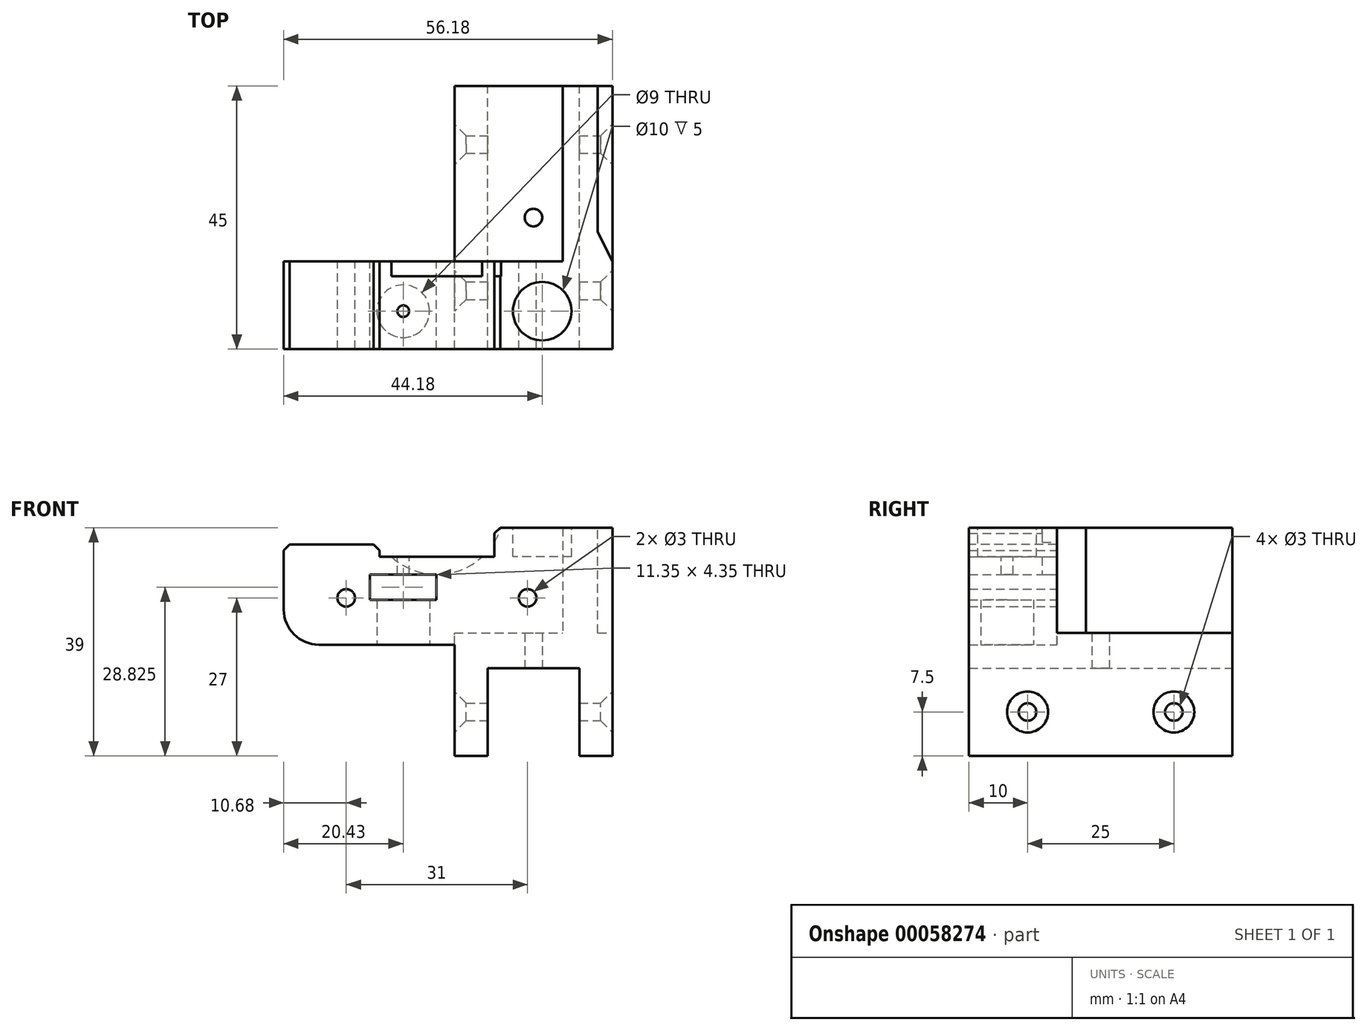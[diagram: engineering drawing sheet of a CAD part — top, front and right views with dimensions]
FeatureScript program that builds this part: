
annotation { "Feature Type Name" : "Feature", "Feature Type Description" : "" }
export const myFeature = defineFeature(function(context is Context, id is Id, definition is map)
    precondition{}
    {
        {
            var Q0;
            Q0=qCreatedBy(makeId("Front.planeOp"),FACE);
            var sketch = newSketch(context, id + "F0", { "sketchPlane" : qUnion([Q0])});
            skLineSegment(sketch, "E0", {"start": v(0, 0) * mm, "end": v(31, 0) * mm, "construction": true});
            skLineSegment(sketch, "E1", {"start": v(0, 0) * mm, "end": v(0, 31) * mm, "construction": true});
            skPoint(sketch, "E2", {"position": v(0, 10.1) * mm});
            skCircle(sketch, "E3", {"center": v(0, 0) * mm, "radius": 1.5 * mm});
            skCircle(sketch, "E4", {"center": v(31, 0) * mm, "radius": 1.5 * mm});
            skLineSegment(sketch, "E5", {"start": v(15.5, 0) * mm, "end": v(15.5, 31) * mm, "construction": true});
            skLineSegment(sketch, "E6", {"start": v(9.75, 0) * mm, "end": v(9.75, 33.75) * mm, "construction": true});
            skArc(sketch, "E7", {"start": v(0, 10.1) * mm, "mid": v(17.8, 20.04) * mm, "end": v(18.66, 40.41) * mm, "construction": true});
            skLineSegment(sketch, "E8", {"start": v(33.5, 41.53) * mm, "end": v(33.5, -19.25) * mm, "construction": true});
            skCircle(sketch, "E9", {"center": v(15.5, 15.5) * mm, "radius": 7.5 * mm, "construction": true});
            skLineSegment(sketch, "E10", {"start": v(-10.68, 9.1) * mm, "end": v(5.67, 9.1) * mm});
            skLineSegment(sketch, "E11", {"start": v(5.67, 9.1) * mm, "end": v(5.67, 7) * mm});
            skLineSegment(sketch, "E12", {"start": v(5.67, 7) * mm, "end": v(25.32, 7) * mm});
            skLineSegment(sketch, "E13", {"start": v(25.32, 7) * mm, "end": v(25.32, 12) * mm});
            skLineSegment(sketch, "E14", {"start": v(25.32, 12) * mm, "end": v(41.68, 12) * mm});
            skPoint(sketch, "E15", {"position": v(33.5, 12) * mm});
            skLineSegment(sketch, "E16", {"start": v(-10.68, 9.1) * mm, "end": v(-10.68, -8) * mm});
            skLineSegment(sketch, "E17", {"start": v(-10.68, -8) * mm, "end": v(41.68, -8) * mm});
            skLineSegment(sketch, "E18", {"start": v(41.68, -8) * mm, "end": v(41.68, 12) * mm});
            skPoint(sketch, "E19", {"position": v(15.5, 8) * mm});
            skLineSegment(sketch, "E20.bottom", {"start": v(4.08, 4) * mm, "end": v(15.42, 4) * mm});
            skLineSegment(sketch, "E20.top", {"start": v(4.08, -0.35) * mm, "end": v(15.42, -0.35) * mm});
            skLineSegment(sketch, "E20.left", {"start": v(4.08, 4) * mm, "end": v(4.08, -0.35) * mm});
            skLineSegment(sketch, "E20.right", {"start": v(15.43, 4) * mm, "end": v(15.43, -0.35) * mm});
            skSolve(sketch);
        }
        {
            var Q0;
            Q0=qSketchRegion(id+"F0",true);
            extrude(context, id + "F1", {"entities" : qUnion([Q0]), "depth" : 13 * mm, "symmetric" : true});
        }
        {
            var Q0;
            Q0=makeQuery(id+"F1.opExtrude","SWEPT_FACE",FACE,{"disambiguationData":[OSD([sQuery(id+"F0.wireOp",EDGE,"E12")])]});
            var sketch = newSketch(context, id + "F2", { "sketchPlane" : qUnion([Q0])});
            skLineSegment(sketch, "E21.0", {"start": v(4.08, -6.5) * mm, "end": v(15.43, -6.5) * mm, "construction": true});
            skLineSegment(sketch, "E22", {"start": v(9.75, -6.5) * mm, "end": v(9.75, 6.5) * mm, "construction": true});
            skCircle(sketch, "E23", {"center": v(9.75, 0) * mm, "radius": 1 * mm});
            skSolve(sketch);
        }
        {
            var Q0;
            Q0=qSketchRegion(id+"F2",true);
            extrude(context, id + "F3", {"entities" : qUnion([Q0]), "operationType" : NewBodyOperationType.REMOVE, "endBound" : BoundingType.THROUGH_ALL, "oppositeDirection" : true, "depth" : 25 * mm});
        }
        {
            var Q0;
            Q0=makeQuery(id+"F1.opExtrude","SWEPT_FACE",FACE,{"disambiguationData":[OSD([sQuery(id+"F0.wireOp",EDGE,"E17")])]});
            var sketch = newSketch(context, id + "F4", { "sketchPlane" : qUnion([Q0])});
            skCircle(sketch, "E24", {"center": v(9.75, 0) * mm, "radius": 4.5 * mm});
            skSolve(sketch);
        }
        {
            var Q0;
            Q0=qSketchRegion(id+"F4",true);
            var Q1;
            Q1=makeQuery(id+"F1.opExtrude","SWEPT_FACE",FACE,{"disambiguationData":[OSD([sQuery(id+"F0.wireOp",EDGE,"E20.top")])]});
            extrude(context, id + "F5", {"entities" : qUnion([Q0]), "operationType" : NewBodyOperationType.REMOVE, "endBound" : BoundingType.UP_TO_SURFACE, "oppositeDirection" : true, "endBoundEntityFace" : qUnion([Q1]), "depth" : 25 * mm});
        }
        {
            var Q0;
            Q0=makeQuery(id+"F3.boolean.opBoolean","COPY",EDGE,{"derivedFrom":makeQuery(id+"F3.opExtrude","CAP_EDGE",EDGE,{"disambiguationData":[OSD([sQuery(id+"F2.wireOp",EDGE,"E23")])],"isStart":true})});
            var Q1;
            Q1=makeQuery(id+"F5.boolean.opBoolean","COPY",EDGE,{"derivedFrom":makeQuery(id+"F5.opExtrude","CAP_EDGE",EDGE,{"disambiguationData":[OSD([sQuery(id+"F4.wireOp",EDGE,"E24")])],"isStart":true})});
            var Q2;
            Q2=makeQuery(id+"F1.opExtrude","SWEPT_EDGE",EDGE,{"disambiguationData":[OSD([sQuery(id+"F0.wireOp",EDGE,"E10"),sQuery(id+"F0.wireOp",EDGE,"E11")])]});
            var Q3;
            Q3=makeQuery(id+"F1.opExtrude","SWEPT_EDGE",EDGE,{"disambiguationData":[OSD([sQuery(id+"F0.wireOp",EDGE,"E13"),sQuery(id+"F0.wireOp",EDGE,"E14")])]});
            var Q4;
            Q4=makeQuery(id+"F1.opExtrude","SWEPT_EDGE",EDGE,{"disambiguationData":[OSD([sQuery(id+"F0.wireOp",EDGE,"E10"),sQuery(id+"F0.wireOp",EDGE,"E16")])]});
            var Q5;
            Q5=makeQuery(id+"F1.opExtrude","SWEPT_EDGE",EDGE,{"disambiguationData":[OSD([sQuery(id+"F0.wireOp",EDGE,"E14"),sQuery(id+"F0.wireOp",EDGE,"E18")])]});
            chamfer(context, id + "F6", {"entities" : qUnion([Q0, Q1, Q2, Q3, Q4, Q5]), "width" : 1 * mm, "tangentPropagation" : true});
        }
        {
            var Q0;
            Q0=makeQuery(id+"F1.opExtrude","SWEPT_EDGE",EDGE,{"disambiguationData":[OSD([sQuery(id+"F0.wireOp",EDGE,"E16"),sQuery(id+"F0.wireOp",EDGE,"E17")])]});
            var Q1;
            Q1=makeQuery(id+"F1.opExtrude","SWEPT_EDGE",EDGE,{"disambiguationData":[OSD([sQuery(id+"F0.wireOp",EDGE,"E17"),sQuery(id+"F0.wireOp",EDGE,"E18")])]});
            fillet(context, id + "F7", {"entities" : qUnion([Q0, Q1]), "radius" : 6 * mm, "tangentPropagation" : true, "allowEdgeOverflow" : false});
        }
        {
            var Q0;
            Q0=makeQuery(id+"F1.opExtrude","SWEPT_FACE",FACE,{"disambiguationData":[OSD([sQuery(id+"F0.wireOp",EDGE,"E14")])]});
            var sketch = newSketch(context, id + "F8", { "sketchPlane" : qUnion([Q0])});
            skLineSegment(sketch, "E25", {"start": v(33.5, 6.5) * mm, "end": v(33.5, -6.5) * mm, "construction": true});
            skCircle(sketch, "E26", {"center": v(33.5, 0) * mm, "radius": 5 * mm});
            skSolve(sketch);
        }
        {
            var Q0;
            Q0=qSketchRegion(id+"F8",true);
            extrude(context, id + "F9", {"entities" : qUnion([Q0]), "operationType" : NewBodyOperationType.REMOVE, "oppositeDirection" : true, "depth" : 5 * mm});
        }
        {
            var Q0;
            Q0=makeQuery(id+"F1.opExtrude","CAP_FACE",FACE,{"disambiguationData":[OSD([sQuery(id+"F0.wireOp",EDGE,"E3"),sQuery(id+"F0.wireOp",EDGE,"E4"),sQuery(id+"F0.wireOp",EDGE,"E10"),sQuery(id+"F0.wireOp",EDGE,"E11"),sQuery(id+"F0.wireOp",EDGE,"E12"),sQuery(id+"F0.wireOp",EDGE,"E13"),sQuery(id+"F0.wireOp",EDGE,"E14"),sQuery(id+"F0.wireOp",EDGE,"E16"),sQuery(id+"F0.wireOp",EDGE,"E17"),sQuery(id+"F0.wireOp",EDGE,"E18"),sQuery(id+"F0.wireOp",EDGE,"E20.bottom"),sQuery(id+"F0.wireOp",EDGE,"E20.top"),sQuery(id+"F0.wireOp",EDGE,"E20.left"),sQuery(id+"F0.wireOp",EDGE,"E20.right")])],"isStart":true});
            extrude(context, id + "F10", {"entities" : qUnion([Q0]), "operationType" : NewBodyOperationType.ADD, "depth" : 2 * mm});
        }
        {
            var Q0;
            Q0=makeQuery(id+"F10.opExtrude","CAP_FACE",FACE,{"disambiguationData":[OSD([sQuery(id+"F0.wireOp",EDGE,"E3"),sQuery(id+"F0.wireOp",EDGE,"E4"),sQuery(id+"F0.wireOp",EDGE,"E10"),sQuery(id+"F0.wireOp",EDGE,"E11"),sQuery(id+"F0.wireOp",EDGE,"E12"),sQuery(id+"F0.wireOp",EDGE,"E13"),sQuery(id+"F0.wireOp",EDGE,"E14"),sQuery(id+"F0.wireOp",EDGE,"E16"),sQuery(id+"F0.wireOp",EDGE,"E17"),sQuery(id+"F0.wireOp",EDGE,"E18"),sQuery(id+"F0.wireOp",EDGE,"E20.bottom"),sQuery(id+"F0.wireOp",EDGE,"E20.top"),sQuery(id+"F0.wireOp",EDGE,"E20.left"),sQuery(id+"F0.wireOp",EDGE,"E20.right")])],"isStart":false});
            var sketch = newSketch(context, id + "F11", { "sketchPlane" : qUnion([Q0])});
            skLineSegment(sketch, "E27", {"start": v(-31, 0) * mm, "end": v(0, 0) * mm, "construction": true});
            skLineSegment(sketch, "E28", {"start": v(0, 0) * mm, "end": v(0, 31) * mm, "construction": true});
            skLineSegment(sketch, "E29", {"start": v(0, 31) * mm, "end": v(-31, 0) * mm, "construction": true});
            skLineSegment(sketch, "E30.bottom", {"start": v(6, -6) * mm, "end": v(-37, -6) * mm});
            skLineSegment(sketch, "E30.top", {"start": v(6, 37) * mm, "end": v(-37, 37) * mm, "construction": true});
            skLineSegment(sketch, "E30.left", {"start": v(6, -6) * mm, "end": v(6, 37) * mm, "construction": true});
            skLineSegment(sketch, "E30.right", {"start": v(-37, -6) * mm, "end": v(-37, 37) * mm, "construction": true});
            skPoint(sketch, "E30.middle", {"position": v(-15.5, 15.5) * mm});
            skLineSegment(sketch, "E31.0", {"start": v(-41.68, -2) * mm, "end": v(-41.68, 11) * mm});
            skArc(sketch, "E31.1", {"start": v(-41.68, -2) * mm, "mid": v(-39.92, -6.24) * mm, "end": v(-35.68, -8) * mm});
            skLineSegment(sketch, "E31.2", {"start": v(4.68, -8) * mm, "end": v(-35.68, -8) * mm});
            skArc(sketch, "E31.3", {"start": v(4.68, -8) * mm, "mid": v(8.92, -6.24) * mm, "end": v(10.68, -2) * mm});
            skLineSegment(sketch, "E31.4", {"start": v(10.68, 8.1) * mm, "end": v(10.68, -2) * mm});
            skLineSegment(sketch, "E31.5", {"start": v(-37, 12) * mm, "end": v(-40.68, 12) * mm});
            skLineSegment(sketch, "E31.6", {"start": v(-40.68, 12) * mm, "end": v(-41.68, 11) * mm});
            skLineSegment(sketch, "E31.7", {"start": v(10.68, 8.1) * mm, "end": v(9.68, 9.1) * mm});
            skLineSegment(sketch, "E31.8", {"start": v(9.68, 9.1) * mm, "end": v(6, 9.1) * mm});
            skPoint(sketch, "E32.orphan", {"position": v(-26.33, 12) * mm});
            skPoint(sketch, "E33.orphan", {"position": v(-4.67, 9.1) * mm});
            skLineSegment(sketch, "E34", {"start": v(-37, 12) * mm, "end": v(-37, -6) * mm});
            skLineSegment(sketch, "E35", {"start": v(6, 9.1) * mm, "end": v(6, -6) * mm});
            skSolve(sketch);
        }
        {
            var Q0;
            Q0 = qSketchRegion(id + "F11", true);
            extrude(context, id + "F12", {"entities" : qUnion([Q0]), "operationType" : NewBodyOperationType.ADD, "depth" : 30 * mm});
        }
        {
            var Q0;
            Q0=makeQuery(id+"F12.opExtrude","CAP_FACE",FACE,{"disambiguationData":[OSD([sQuery(id+"F11.wireOp",EDGE,"E30.bottom"),sQuery(id+"F11.wireOp",EDGE,"E31.0"),sQuery(id+"F11.wireOp",EDGE,"E31.1"),sQuery(id+"F11.wireOp",EDGE,"E31.2"),sQuery(id+"F11.wireOp",EDGE,"E31.3"),sQuery(id+"F11.wireOp",EDGE,"E31.4"),sQuery(id+"F11.wireOp",EDGE,"E31.5"),sQuery(id+"F11.wireOp",EDGE,"E31.6"),sQuery(id+"F11.wireOp",EDGE,"E31.7"),sQuery(id+"F11.wireOp",EDGE,"E31.8"),sQuery(id+"F11.wireOp",EDGE,"E34"),sQuery(id+"F11.wireOp",EDGE,"E35")])],"isStart":false});
            var sketch = newSketch(context, id + "F13", { "sketchPlane" : qUnion([Q0])});
            skLineSegment(sketch, "E36.0", {"start": v(-15.25, -8) * mm, "end": v(-4.25, -8) * mm, "construction": true});
            skArc(sketch, "E37.0", {"start": v(-41.68, -2) * mm, "mid": v(-39.92, -6.24) * mm, "end": v(-35.68, -8) * mm});
            skLineSegment(sketch, "E38", {"start": v(-41.68, -2) * mm, "end": v(-41.68, -12) * mm});
            skLineSegment(sketch, "E39", {"start": v(-41.68, -12) * mm, "end": v(-18.5, -12) * mm});
            skLineSegment(sketch, "E40", {"start": v(-18.5, -12) * mm, "end": v(-18.5, -8) * mm});
            skLineSegment(sketch, "E41", {"start": v(-18.5, -8) * mm, "end": v(-35.68, -8) * mm});
            skSolve(sketch);
        }
        {
            var Q0;
            Q0 = qSketchRegion(id + "F13", true);
            var Q1;
            Q1=makeQuery(id+"F1.opExtrude","CAP_FACE",FACE,{"disambiguationData":[OSD([sQuery(id+"F0.wireOp",EDGE,"E3"),sQuery(id+"F0.wireOp",EDGE,"E4"),sQuery(id+"F0.wireOp",EDGE,"E10"),sQuery(id+"F0.wireOp",EDGE,"E11"),sQuery(id+"F0.wireOp",EDGE,"E12"),sQuery(id+"F0.wireOp",EDGE,"E13"),sQuery(id+"F0.wireOp",EDGE,"E14"),sQuery(id+"F0.wireOp",EDGE,"E16"),sQuery(id+"F0.wireOp",EDGE,"E17"),sQuery(id+"F0.wireOp",EDGE,"E18"),sQuery(id+"F0.wireOp",EDGE,"E20.bottom"),sQuery(id+"F0.wireOp",EDGE,"E20.top"),sQuery(id+"F0.wireOp",EDGE,"E20.left"),sQuery(id+"F0.wireOp",EDGE,"E20.right")])],"isStart":false});
            extrude(context, id + "F14", {"entities" : qUnion([Q0]), "operationType" : NewBodyOperationType.ADD, "endBound" : BoundingType.UP_TO_SURFACE, "oppositeDirection" : true, "endBoundEntityFace" : qUnion([Q1]), "depth" : 25 * mm});
        }
        {
            var Q0;
            {var subQ0=sQuery(id+"F0.wireOp",EDGE,"E20.right");var subQ1=sQuery(id+"F0.wireOp",EDGE,"E20.left");var subQ2=sQuery(id+"F0.wireOp",EDGE,"E20.top");var subQ3=sQuery(id+"F0.wireOp",EDGE,"E20.bottom");var subQ4=sQuery(id+"F0.wireOp",EDGE,"E18");var subQ5=sQuery(id+"F0.wireOp",EDGE,"E17");var subQ6=sQuery(id+"F0.wireOp",EDGE,"E16");var subQ7=sQuery(id+"F0.wireOp",EDGE,"E14");var subQ8=sQuery(id+"F0.wireOp",EDGE,"E13");var subQ9=sQuery(id+"F0.wireOp",EDGE,"E12");var subQ10=sQuery(id+"F0.wireOp",EDGE,"E11");var subQ11=sQuery(id+"F0.wireOp",EDGE,"E10");var subQ12=sQuery(id+"F0.wireOp",EDGE,"E4");var subQ13=sQuery(id+"F0.wireOp",EDGE,"E3");Q0=makeQuery(id+"F14.boolean.opBoolean","MERGE",FACE,{"derivedFrom":[makeQuery(id+"F1.opExtrude","CAP_FACE",FACE,{"disambiguationData":[OSD([subQ13,subQ12,subQ11,subQ10,subQ9,subQ8,subQ7,subQ6,subQ5,subQ4,subQ3,subQ2,subQ1,subQ0])],"isStart":false}),makeQuery(id+"F14.opExtrude","CAP_FACE",FACE,{"disambiguationData":[OSD([subQ13,subQ12,subQ11,subQ10,subQ9,subQ8,subQ7,subQ6,subQ5,subQ4,subQ3,subQ2,subQ1,subQ0])],"isStart":false})]});}
            var sketch = newSketch(context, id + "F15", { "sketchPlane" : qUnion([Q0])});
            skLineSegment(sketch, "E42", {"start": v(40.68, 12) * mm, "end": v(41.68, 11) * mm});
            skLineSegment(sketch, "E43", {"start": v(41.68, 11) * mm, "end": v(41.68, -12) * mm});
            skLineSegment(sketch, "E44", {"start": v(41.68, -12) * mm, "end": v(45.5, -12) * mm});
            skLineSegment(sketch, "E45", {"start": v(45.5, -12) * mm, "end": v(45.5, 12) * mm});
            skLineSegment(sketch, "E46", {"start": v(45.5, 12) * mm, "end": v(40.68, 12) * mm});
            skSolve(sketch);
        }
        {
            var Q0;
            Q0 = qSketchRegion(id + "F15", true);
            var Q1;
            Q1=makeQuery(id+"F14.boolean.opBoolean","MERGE",FACE,{"derivedFrom":[makeQuery(id+"F12.opExtrude","CAP_FACE",FACE,{"disambiguationData":[OSD([sQuery(id+"F11.wireOp",EDGE,"E30.bottom"),sQuery(id+"F11.wireOp",EDGE,"E31.0"),sQuery(id+"F11.wireOp",EDGE,"E31.1"),sQuery(id+"F11.wireOp",EDGE,"E31.2"),sQuery(id+"F11.wireOp",EDGE,"E31.3"),sQuery(id+"F11.wireOp",EDGE,"E31.4"),sQuery(id+"F11.wireOp",EDGE,"E31.5"),sQuery(id+"F11.wireOp",EDGE,"E31.6"),sQuery(id+"F11.wireOp",EDGE,"E31.7"),sQuery(id+"F11.wireOp",EDGE,"E31.8"),sQuery(id+"F11.wireOp",EDGE,"E34"),sQuery(id+"F11.wireOp",EDGE,"E35")])],"isStart":false}),makeQuery(id+"F14.opExtrude","CAP_FACE",FACE,{"disambiguationData":[OSD([sQuery(id+"F13.wireOp",EDGE,"E37.0"),sQuery(id+"F13.wireOp",EDGE,"E38"),sQuery(id+"F13.wireOp",EDGE,"E39"),sQuery(id+"F13.wireOp",EDGE,"E40"),sQuery(id+"F13.wireOp",EDGE,"E41")])],"isStart":true})]});
            extrude(context, id + "F16", {"entities" : qUnion([Q0]), "operationType" : NewBodyOperationType.ADD, "endBound" : BoundingType.UP_TO_SURFACE, "oppositeDirection" : true, "endBoundEntityFace" : qUnion([Q1]), "depth" : 25 * mm});
        }
        {
            var Q0;
            {var subQ0=sQuery(id+"F0.wireOp",EDGE,"E20.right");var subQ1=sQuery(id+"F0.wireOp",EDGE,"E20.left");var subQ2=sQuery(id+"F0.wireOp",EDGE,"E20.top");var subQ3=sQuery(id+"F0.wireOp",EDGE,"E20.bottom");var subQ4=sQuery(id+"F0.wireOp",EDGE,"E18");var subQ5=sQuery(id+"F0.wireOp",EDGE,"E17");var subQ6=sQuery(id+"F0.wireOp",EDGE,"E16");var subQ7=sQuery(id+"F0.wireOp",EDGE,"E14");var subQ8=sQuery(id+"F0.wireOp",EDGE,"E13");var subQ9=sQuery(id+"F0.wireOp",EDGE,"E12");var subQ10=sQuery(id+"F0.wireOp",EDGE,"E11");var subQ11=sQuery(id+"F0.wireOp",EDGE,"E10");var subQ12=sQuery(id+"F0.wireOp",EDGE,"E4");var subQ13=sQuery(id+"F0.wireOp",EDGE,"E3");Q0=makeQuery(id+"F16.boolean.opBoolean","MERGE",FACE,{"derivedFrom":[makeQuery(id+"F14.boolean.opBoolean","MERGE",FACE,{"derivedFrom":[makeQuery(id+"F1.opExtrude","CAP_FACE",FACE,{"disambiguationData":[OSD([subQ13,subQ12,subQ11,subQ10,subQ9,subQ8,subQ7,subQ6,subQ5,subQ4,subQ3,subQ2,subQ1,subQ0])],"isStart":false}),makeQuery(id+"F14.opExtrude","CAP_FACE",FACE,{"disambiguationData":[OSD([subQ13,subQ12,subQ11,subQ10,subQ9,subQ8,subQ7,subQ6,subQ5,subQ4,subQ3,subQ2,subQ1,subQ0])],"isStart":false})]}),makeQuery(id+"F16.opExtrude","CAP_FACE",FACE,{"disambiguationData":[OSD([sQuery(id+"F15.wireOp",EDGE,"E42"),sQuery(id+"F15.wireOp",EDGE,"E43"),sQuery(id+"F15.wireOp",EDGE,"E44"),sQuery(id+"F15.wireOp",EDGE,"E45"),sQuery(id+"F15.wireOp",EDGE,"E46")])],"isStart":true})]});}
            var sketch = newSketch(context, id + "F17", { "sketchPlane" : qUnion([Q0])});
            skLineSegment(sketch, "E47.bottom", {"start": v(18.5, -12) * mm, "end": v(24.5, -12) * mm});
            skLineSegment(sketch, "E47.top", {"start": v(18.5, -27) * mm, "end": v(24.5, -27) * mm});
            skLineSegment(sketch, "E47.left", {"start": v(18.5, -12) * mm, "end": v(18.5, -27) * mm});
            skLineSegment(sketch, "E47.right", {"start": v(24.5, -12) * mm, "end": v(24.5, -27) * mm});
            skLineSegment(sketch, "E48.bottom", {"start": v(45.5, -12) * mm, "end": v(39.5, -12) * mm});
            skLineSegment(sketch, "E48.top", {"start": v(45.5, -27) * mm, "end": v(39.5, -27) * mm});
            skLineSegment(sketch, "E48.left", {"start": v(45.5, -12) * mm, "end": v(45.5, -27) * mm});
            skLineSegment(sketch, "E48.right", {"start": v(39.5, -12) * mm, "end": v(39.5, -27) * mm});
            skSolve(sketch);
        }
        {
            var Q0;
            Q0 = qSketchRegion(id + "F17", true);
            var Q1;
            {var subQ0=sQuery(id+"F13.wireOp",EDGE,"E41");var subQ1=sQuery(id+"F13.wireOp",EDGE,"E40");var subQ2=sQuery(id+"F13.wireOp",EDGE,"E39");var subQ3=sQuery(id+"F13.wireOp",EDGE,"E38");var subQ4=sQuery(id+"F13.wireOp",EDGE,"E37.0");var subQ5=sQuery(id+"F11.wireOp",EDGE,"E35");var subQ6=sQuery(id+"F11.wireOp",EDGE,"E34");var subQ7=sQuery(id+"F11.wireOp",EDGE,"E31.8");var subQ8=sQuery(id+"F11.wireOp",EDGE,"E31.7");var subQ9=sQuery(id+"F11.wireOp",EDGE,"E31.6");var subQ10=sQuery(id+"F11.wireOp",EDGE,"E31.5");var subQ11=sQuery(id+"F11.wireOp",EDGE,"E31.4");var subQ12=sQuery(id+"F11.wireOp",EDGE,"E31.3");var subQ13=sQuery(id+"F11.wireOp",EDGE,"E31.2");var subQ14=sQuery(id+"F11.wireOp",EDGE,"E31.1");var subQ15=sQuery(id+"F11.wireOp",EDGE,"E31.0");var subQ16=sQuery(id+"F11.wireOp",EDGE,"E30.bottom");Q1=makeQuery(id+"F16.boolean.opBoolean","MERGE",FACE,{"derivedFrom":[makeQuery(id+"F14.boolean.opBoolean","MERGE",FACE,{"derivedFrom":[makeQuery(id+"F12.opExtrude","CAP_FACE",FACE,{"disambiguationData":[OSD([subQ16,subQ15,subQ14,subQ13,subQ12,subQ11,subQ10,subQ9,subQ8,subQ7,subQ6,subQ5])],"isStart":false}),makeQuery(id+"F14.opExtrude","CAP_FACE",FACE,{"disambiguationData":[OSD([subQ4,subQ3,subQ2,subQ1,subQ0])],"isStart":true})]}),makeQuery(id+"F16.opExtrude","CAP_FACE",FACE,{"disambiguationData":[OSD([subQ16,subQ15,subQ14,subQ13,subQ12,subQ11,subQ10,subQ9,subQ8,subQ7,subQ6,subQ5,subQ4,subQ3,subQ2,subQ1,subQ0])],"isStart":false})]});}
            extrude(context, id + "F18", {"entities" : qUnion([Q0]), "operationType" : NewBodyOperationType.ADD, "endBound" : BoundingType.UP_TO_SURFACE, "oppositeDirection" : true, "endBoundEntityFace" : qUnion([Q1]), "depth" : 25 * mm});
        }
        {
            var Q0;
            Q0=makeQuery(id+"F16.boolean.opBoolean","MERGE",FACE,{"derivedFrom":[makeQuery(id+"F14.opExtrude","SWEPT_FACE",FACE,{"disambiguationData":[OSD([sQuery(id+"F13.wireOp",EDGE,"E39")])]}),makeQuery(id+"F16.opExtrude","SWEPT_FACE",FACE,{"disambiguationData":[OSD([sQuery(id+"F15.wireOp",EDGE,"E44")])]})]});
            var sketch = newSketch(context, id + "F19", { "sketchPlane" : qUnion([Q0])});
            skLineSegment(sketch, "E49.0", {"start": v(-6, -8.5) * mm, "end": v(37, -8.5) * mm, "construction": true});
            skLineSegment(sketch, "E50", {"start": v(32, -38.5) * mm, "end": v(32, 6.5) * mm, "construction": true});
            skCircle(sketch, "E51", {"center": v(32, -16) * mm, "radius": 1.5 * mm});
            skSolve(sketch);
        }
        {
            var Q0;
            Q0 = qSketchRegion(id + "F19", true);
            extrude(context, id + "F20", {"entities" : qUnion([Q0]), "operationType" : NewBodyOperationType.REMOVE, "endBound" : BoundingType.UP_TO_NEXT, "oppositeDirection" : true, "depth" : 25 * mm});
        }
        {
            var Q0;
            Q0=makeQuery(id+"F18.opExtrude","SWEPT_FACE",FACE,{"disambiguationData":[OSD([sQuery(id+"F17.wireOp",EDGE,"E47.right")])]});
            var sketch = newSketch(context, id + "F21", { "sketchPlane" : qUnion([Q0])});
            skLineSegment(sketch, "E52", {"start": v(-6.5, -19.5) * mm, "end": v(38.5, -19.5) * mm, "construction": true});
            skCircle(sketch, "E53", {"center": v(3.5, -19.5) * mm, "radius": 1.5 * mm});
            skCircle(sketch, "E54", {"center": v(28.5, -19.5) * mm, "radius": 1.5 * mm});
            skSolve(sketch);
        }
        {
            var Q0;
            Q0 = qSketchRegion(id + "F21", true);
            extrude(context, id + "F22", {"entities" : qUnion([Q0]), "operationType" : NewBodyOperationType.REMOVE, "endBound" : BoundingType.THROUGH_ALL, "oppositeDirection" : true, "depth" : 25 * mm, "hasSecondDirection" : true, "secondDirectionBound" : BoundingType.THROUGH_ALL, "secondDirectionOppositeDirection" : false, "secondDirectionDepth" : 25 * mm});
        }
        {
            var Q0;
            Q0=makeQuery(id+"F22.boolean.opBoolean","INTERSECT",EDGE,{"derivedFrom":[makeQuery(id+"F18.boolean.opBoolean","MERGE",FACE,{"derivedFrom":[makeQuery(id+"F14.opExtrude","SWEPT_FACE",FACE,{"disambiguationData":[OSD([sQuery(id+"F13.wireOp",EDGE,"E40")])]}),makeQuery(id+"F18.opExtrude","SWEPT_FACE",FACE,{"disambiguationData":[OSD([sQuery(id+"F17.wireOp",EDGE,"E47.left")])]})]}),makeQuery(id+"F22.opExtrude","SWEPT_FACE",FACE,{"disambiguationData":[OSD([sQuery(id+"F21.wireOp",EDGE,"E54")])]})]});
            var Q1;
            Q1=makeQuery(id+"F22.boolean.opBoolean","INTERSECT",EDGE,{"derivedFrom":[makeQuery(id+"F18.boolean.opBoolean","MERGE",FACE,{"derivedFrom":[makeQuery(id+"F14.opExtrude","SWEPT_FACE",FACE,{"disambiguationData":[OSD([sQuery(id+"F13.wireOp",EDGE,"E40")])]}),makeQuery(id+"F18.opExtrude","SWEPT_FACE",FACE,{"disambiguationData":[OSD([sQuery(id+"F17.wireOp",EDGE,"E47.left")])]})]}),makeQuery(id+"F22.opExtrude","SWEPT_FACE",FACE,{"disambiguationData":[OSD([sQuery(id+"F21.wireOp",EDGE,"E53")])]})]});
            var Q2;
            Q2=makeQuery(id+"F22.boolean.opBoolean","INTERSECT",EDGE,{"derivedFrom":[makeQuery(id+"F18.boolean.opBoolean","MERGE",FACE,{"derivedFrom":[makeQuery(id+"F16.opExtrude","SWEPT_FACE",FACE,{"disambiguationData":[OSD([sQuery(id+"F15.wireOp",EDGE,"E45")])]}),makeQuery(id+"F18.opExtrude","SWEPT_FACE",FACE,{"disambiguationData":[OSD([sQuery(id+"F17.wireOp",EDGE,"E48.left")])]})]}),makeQuery(id+"F22.opExtrude","SWEPT_FACE",FACE,{"disambiguationData":[OSD([sQuery(id+"F21.wireOp",EDGE,"E54")])]})]});
            var Q3;
            Q3=makeQuery(id+"F22.boolean.opBoolean","INTERSECT",EDGE,{"derivedFrom":[makeQuery(id+"F18.boolean.opBoolean","MERGE",FACE,{"derivedFrom":[makeQuery(id+"F16.opExtrude","SWEPT_FACE",FACE,{"disambiguationData":[OSD([sQuery(id+"F15.wireOp",EDGE,"E45")])]}),makeQuery(id+"F18.opExtrude","SWEPT_FACE",FACE,{"disambiguationData":[OSD([sQuery(id+"F17.wireOp",EDGE,"E48.left")])]})]}),makeQuery(id+"F22.opExtrude","SWEPT_FACE",FACE,{"disambiguationData":[OSD([sQuery(id+"F21.wireOp",EDGE,"E53")])]})]});
            var Q4;
            Q4=makeQuery(id+"F20.boolean.opBoolean","COPY",EDGE,{"derivedFrom":makeQuery(id+"F20.opExtrude","TWEAK_EDGE",EDGE,{"derivedFrom":[makeQuery(id+"F12.opExtrude","SWEPT_FACE",FACE,{"disambiguationData":[OSD([sQuery(id+"F11.wireOp",EDGE,"E30.bottom")])]}),makeQuery(id+"F19.imprint","IMPRINT",EDGE,{"derivedFrom":sQuery(id+"F19.wireOp",EDGE,"E51")})]})});
            chamfer(context, id + "F23", {"entities" : qUnion([Q0, Q1, Q2, Q3, Q4]), "width" : 2 * mm, "tangentPropagation" : true});
        }
        {
            var Q0;
            {var subQ0=sQuery(id+"F13.wireOp",EDGE,"E41");var subQ1=sQuery(id+"F13.wireOp",EDGE,"E40");var subQ2=sQuery(id+"F13.wireOp",EDGE,"E39");var subQ3=sQuery(id+"F13.wireOp",EDGE,"E38");var subQ4=sQuery(id+"F13.wireOp",EDGE,"E37.0");var subQ5=sQuery(id+"F11.wireOp",EDGE,"E35");var subQ6=sQuery(id+"F11.wireOp",EDGE,"E34");var subQ7=sQuery(id+"F11.wireOp",EDGE,"E31.8");var subQ8=sQuery(id+"F11.wireOp",EDGE,"E31.7");var subQ9=sQuery(id+"F11.wireOp",EDGE,"E31.6");var subQ10=sQuery(id+"F11.wireOp",EDGE,"E31.5");var subQ11=sQuery(id+"F11.wireOp",EDGE,"E31.4");var subQ12=sQuery(id+"F11.wireOp",EDGE,"E31.3");var subQ13=sQuery(id+"F11.wireOp",EDGE,"E31.2");var subQ14=sQuery(id+"F11.wireOp",EDGE,"E31.1");var subQ15=sQuery(id+"F11.wireOp",EDGE,"E31.0");var subQ16=sQuery(id+"F11.wireOp",EDGE,"E30.bottom");Q0=makeQuery(id+"F18.boolean.opBoolean","MERGE",FACE,{"derivedFrom":[makeQuery(id+"F16.boolean.opBoolean","MERGE",FACE,{"derivedFrom":[makeQuery(id+"F14.boolean.opBoolean","MERGE",FACE,{"derivedFrom":[makeQuery(id+"F12.opExtrude","CAP_FACE",FACE,{"disambiguationData":[OSD([subQ16,subQ15,subQ14,subQ13,subQ12,subQ11,subQ10,subQ9,subQ8,subQ7,subQ6,subQ5])],"isStart":false}),makeQuery(id+"F14.opExtrude","CAP_FACE",FACE,{"disambiguationData":[OSD([subQ4,subQ3,subQ2,subQ1,subQ0])],"isStart":true})]}),makeQuery(id+"F16.opExtrude","CAP_FACE",FACE,{"disambiguationData":[OSD([subQ16,subQ15,subQ14,subQ13,subQ12,subQ11,subQ10,subQ9,subQ8,subQ7,subQ6,subQ5,subQ4,subQ3,subQ2,subQ1,subQ0])],"isStart":false})]}),makeQuery(id+"F18.opExtrude","CAP_FACE",FACE,{"disambiguationData":[OSD([subQ16,subQ15,subQ14,subQ13,subQ12,subQ11,subQ10,subQ9,subQ8,subQ7,subQ6,subQ5,subQ4,subQ3,subQ2,subQ1,subQ0]),ownerDisambiguation([makeQuery(id+"F17.imprint","IMPRINT",EDGE,{"derivedFrom":sQuery(id+"F17.wireOp",EDGE,"E47.bottom")})])],"isStart":false}),makeQuery(id+"F18.opExtrude","CAP_FACE",FACE,{"disambiguationData":[OSD([subQ16,subQ15,subQ14,subQ13,subQ12,subQ11,subQ10,subQ9,subQ8,subQ7,subQ6,subQ5,subQ4,subQ3,subQ2,subQ1,subQ0]),ownerDisambiguation([makeQuery(id+"F17.imprint","IMPRINT",EDGE,{"derivedFrom":sQuery(id+"F17.wireOp",EDGE,"E48.bottom")})])],"isStart":false})]});}
            var sketch = newSketch(context, id + "F24", { "sketchPlane" : qUnion([Q0])});
            skLineSegment(sketch, "E55", {"start": v(-32, -12) * mm, "end": v(-32, -27) * mm, "construction": true});
            skLineSegment(sketch, "E56.bottom", {"start": v(-24.15, -12) * mm, "end": v(-39.85, -12) * mm});
            skLineSegment(sketch, "E56.top", {"start": v(-24.15, -27) * mm, "end": v(-39.85, -27) * mm});
            skLineSegment(sketch, "E56.left", {"start": v(-24.15, -12) * mm, "end": v(-24.15, -27) * mm});
            skLineSegment(sketch, "E56.right", {"start": v(-39.85, -12) * mm, "end": v(-39.85, -27) * mm});
            skPoint(sketch, "E56.middle", {"position": v(-32, -19.5) * mm});
            skSolve(sketch);
        }
        {
            var Q0;
            Q0 = qSketchRegion(id + "F24", true);
            extrude(context, id + "F25", {"entities" : qUnion([Q0]), "operationType" : NewBodyOperationType.REMOVE, "endBound" : BoundingType.THROUGH_ALL, "oppositeDirection" : true, "depth" : 25 * mm});
        }
        {
            var Q0;
            {var subQ0=sQuery(id+"F13.wireOp",EDGE,"E41");var subQ1=sQuery(id+"F13.wireOp",EDGE,"E40");var subQ2=sQuery(id+"F13.wireOp",EDGE,"E39");var subQ3=sQuery(id+"F13.wireOp",EDGE,"E38");var subQ4=sQuery(id+"F13.wireOp",EDGE,"E37.0");var subQ5=sQuery(id+"F11.wireOp",EDGE,"E35");var subQ6=sQuery(id+"F11.wireOp",EDGE,"E34");var subQ7=sQuery(id+"F11.wireOp",EDGE,"E31.8");var subQ8=sQuery(id+"F11.wireOp",EDGE,"E31.7");var subQ9=sQuery(id+"F11.wireOp",EDGE,"E31.6");var subQ10=sQuery(id+"F11.wireOp",EDGE,"E31.5");var subQ11=sQuery(id+"F11.wireOp",EDGE,"E31.4");var subQ12=sQuery(id+"F11.wireOp",EDGE,"E31.3");var subQ13=sQuery(id+"F11.wireOp",EDGE,"E31.2");var subQ14=sQuery(id+"F11.wireOp",EDGE,"E31.1");var subQ15=sQuery(id+"F11.wireOp",EDGE,"E31.0");var subQ16=sQuery(id+"F11.wireOp",EDGE,"E30.bottom");Q0=makeQuery(id+"F18.boolean.opBoolean","MERGE",FACE,{"derivedFrom":[makeQuery(id+"F16.boolean.opBoolean","MERGE",FACE,{"derivedFrom":[makeQuery(id+"F14.boolean.opBoolean","MERGE",FACE,{"derivedFrom":[makeQuery(id+"F12.opExtrude","CAP_FACE",FACE,{"disambiguationData":[OSD([subQ16,subQ15,subQ14,subQ13,subQ12,subQ11,subQ10,subQ9,subQ8,subQ7,subQ6,subQ5])],"isStart":false}),makeQuery(id+"F14.opExtrude","CAP_FACE",FACE,{"disambiguationData":[OSD([subQ4,subQ3,subQ2,subQ1,subQ0])],"isStart":true})]}),makeQuery(id+"F16.opExtrude","CAP_FACE",FACE,{"disambiguationData":[OSD([subQ16,subQ15,subQ14,subQ13,subQ12,subQ11,subQ10,subQ9,subQ8,subQ7,subQ6,subQ5,subQ4,subQ3,subQ2,subQ1,subQ0])],"isStart":false})]}),makeQuery(id+"F18.opExtrude","CAP_FACE",FACE,{"disambiguationData":[OSD([subQ16,subQ15,subQ14,subQ13,subQ12,subQ11,subQ10,subQ9,subQ8,subQ7,subQ6,subQ5,subQ4,subQ3,subQ2,subQ1,subQ0]),ownerDisambiguation([makeQuery(id+"F17.imprint","IMPRINT",EDGE,{"derivedFrom":sQuery(id+"F17.wireOp",EDGE,"E47.bottom")})])],"isStart":false}),makeQuery(id+"F18.opExtrude","CAP_FACE",FACE,{"disambiguationData":[OSD([subQ16,subQ15,subQ14,subQ13,subQ12,subQ11,subQ10,subQ9,subQ8,subQ7,subQ6,subQ5,subQ4,subQ3,subQ2,subQ1,subQ0]),ownerDisambiguation([makeQuery(id+"F17.imprint","IMPRINT",EDGE,{"derivedFrom":sQuery(id+"F17.wireOp",EDGE,"E48.bottom")})])],"isStart":false})]});}
            var sketch = newSketch(context, id + "F26", { "sketchPlane" : qUnion([Q0])});
            skLineSegment(sketch, "E57.bottom", {"start": v(-18.5, -8) * mm, "end": v(10.68, -8) * mm});
            skLineSegment(sketch, "E57.top", {"start": v(-18.5, 9.1) * mm, "end": v(10.68, 9.1) * mm});
            skLineSegment(sketch, "E57.left", {"start": v(-18.5, -8) * mm, "end": v(-18.5, 9.1) * mm});
            skLineSegment(sketch, "E57.right", {"start": v(10.68, -8) * mm, "end": v(10.68, 9.1) * mm});
            skSolve(sketch);
        }
        {
            var Q0;
            Q0 = qSketchRegion(id + "F26", true);
            var Q1;
            Q1=makeQuery(id+"F10.opExtrude","CAP_FACE",FACE,{"disambiguationData":[OSD([sQuery(id+"F0.wireOp",EDGE,"E3"),sQuery(id+"F0.wireOp",EDGE,"E4"),sQuery(id+"F0.wireOp",EDGE,"E10"),sQuery(id+"F0.wireOp",EDGE,"E11"),sQuery(id+"F0.wireOp",EDGE,"E12"),sQuery(id+"F0.wireOp",EDGE,"E13"),sQuery(id+"F0.wireOp",EDGE,"E14"),sQuery(id+"F0.wireOp",EDGE,"E16"),sQuery(id+"F0.wireOp",EDGE,"E17"),sQuery(id+"F0.wireOp",EDGE,"E18"),sQuery(id+"F0.wireOp",EDGE,"E20.bottom"),sQuery(id+"F0.wireOp",EDGE,"E20.top"),sQuery(id+"F0.wireOp",EDGE,"E20.left"),sQuery(id+"F0.wireOp",EDGE,"E20.right")])],"isStart":false});
            extrude(context, id + "F27", {"entities" : qUnion([Q0]), "operationType" : NewBodyOperationType.REMOVE, "endBound" : BoundingType.UP_TO_SURFACE, "oppositeDirection" : true, "endBoundEntityFace" : qUnion([Q1]), "depth" : 25 * mm});
        }
        {
            var Q0;
            {var subQ0=sQuery(id+"F0.wireOp",EDGE,"E14");Q0=makeQuery(id+"F16.boolean.opBoolean","MERGE",FACE,{"derivedFrom":[makeQuery(id+"F12.boolean.opBoolean","MERGE",FACE,{"derivedFrom":[makeQuery(id+"F10.boolean.opBoolean","MERGE",FACE,{"derivedFrom":[makeQuery(id+"F1.opExtrude","SWEPT_FACE",FACE,{"disambiguationData":[OSD([subQ0])]}),makeQuery(id+"F10.opExtrude","SWEPT_FACE",FACE,{"disambiguationData":[OSD([subQ0])]})]}),makeQuery(id+"F12.opExtrude","SWEPT_FACE",FACE,{"disambiguationData":[OSD([sQuery(id+"F11.wireOp",EDGE,"E31.5")])]})]}),makeQuery(id+"F16.opExtrude","SWEPT_FACE",FACE,{"disambiguationData":[OSD([sQuery(id+"F15.wireOp",EDGE,"E46")])]})]});}
            var sketch = newSketch(context, id + "F28", { "sketchPlane" : qUnion([Q0])});
            skLineSegment(sketch, "E58.bottom", {"start": v(45.5, 38.5) * mm, "end": v(43, 38.5) * mm});
            skLineSegment(sketch, "E58.top", {"start": v(45.5, 8.5) * mm, "end": v(43, 8.5) * mm});
            skLineSegment(sketch, "E58.left", {"start": v(45.5, 38.5) * mm, "end": v(45.5, 8.5) * mm});
            skLineSegment(sketch, "E58.right", {"start": v(43, 38.5) * mm, "end": v(43, 8.5) * mm});
            skSolve(sketch);
        }
        {
            var Q0;
            Q0 = qSketchRegion(id + "F28", true);
            var Q1;
            Q1=makeQuery(id+"F12.opExtrude","SWEPT_FACE",FACE,{"disambiguationData":[OSD([sQuery(id+"F11.wireOp",EDGE,"E30.bottom")])]});
            extrude(context, id + "F29", {"entities" : qUnion([Q0]), "operationType" : NewBodyOperationType.REMOVE, "endBound" : BoundingType.UP_TO_SURFACE, "oppositeDirection" : true, "endBoundEntityFace" : qUnion([Q1]), "depth" : 25 * mm});
        }
        {
            var Q0;
            Q0=makeQuery(id+"F29.boolean.opBoolean","COPY",EDGE,{"derivedFrom":makeQuery(id+"F29.opExtrude","SWEPT_EDGE",EDGE,{"disambiguationData":[OSD([sQuery(id+"F28.wireOp",EDGE,"E58.top"),sQuery(id+"F28.wireOp",EDGE,"E58.right")])]})});
            var Q1;
            Q1=makeQuery(id+"F29.boolean.opBoolean","COPY",EDGE,{"derivedFrom":makeQuery(id+"F29.opExtrude","TWEAK_EDGE",EDGE,{"derivedFrom":[makeQuery(id+"F12.opExtrude","SWEPT_FACE",FACE,{"disambiguationData":[OSD([sQuery(id+"F11.wireOp",EDGE,"E30.bottom")])]}),makeQuery(id+"F28.imprint","IMPRINT",EDGE,{"derivedFrom":sQuery(id+"F28.wireOp",EDGE,"E58.right")})]})});
            chamfer(context, id + "F30", {"entities" : qUnion([Q0, Q1]), "chamferType" : ChamferType.TWO_OFFSETS, "width1" : 2.5 * mm, "oppositeDirection" : false, "width2" : 5 * mm, "tangentPropagation" : true});
        }
        {
            var Q0;
            {var subQ0=sQuery(id+"F0.wireOp",EDGE,"E20.right");var subQ1=sQuery(id+"F0.wireOp",EDGE,"E20.left");var subQ2=sQuery(id+"F0.wireOp",EDGE,"E20.top");var subQ3=sQuery(id+"F0.wireOp",EDGE,"E20.bottom");var subQ4=sQuery(id+"F0.wireOp",EDGE,"E18");var subQ5=sQuery(id+"F0.wireOp",EDGE,"E17");var subQ6=sQuery(id+"F0.wireOp",EDGE,"E16");var subQ7=sQuery(id+"F0.wireOp",EDGE,"E14");var subQ8=sQuery(id+"F0.wireOp",EDGE,"E13");var subQ9=sQuery(id+"F0.wireOp",EDGE,"E12");var subQ10=sQuery(id+"F0.wireOp",EDGE,"E11");var subQ11=sQuery(id+"F0.wireOp",EDGE,"E10");var subQ12=sQuery(id+"F0.wireOp",EDGE,"E4");var subQ13=sQuery(id+"F0.wireOp",EDGE,"E3");Q0=makeQuery(id+"F27.boolean.opBoolean","MERGE",FACE,{"derivedFrom":[makeQuery(id+"F10.opExtrude","CAP_FACE",FACE,{"disambiguationData":[OSD([subQ13,subQ12,subQ11,subQ10,subQ9,subQ8,subQ7,subQ6,subQ5,subQ4,subQ3,subQ2,subQ1,subQ0])],"isStart":false}),makeQuery(id+"F27.opExtrude","CAP_FACE",FACE,{"disambiguationData":[OSD([subQ13,subQ12,subQ11,subQ10,subQ9,subQ8,subQ7,subQ6,subQ5,subQ4,subQ3,subQ2,subQ1,subQ0])],"isStart":false})]});}
            var sketch = newSketch(context, id + "F31", { "sketchPlane" : qUnion([Q0])});
            skLineSegment(sketch, "E59", {"start": v(-31, 0) * mm, "end": v(0, 0) * mm, "construction": true});
            skLineSegment(sketch, "E60", {"start": v(0, 0) * mm, "end": v(0, 31) * mm, "construction": true});
            skLineSegment(sketch, "E61", {"start": v(0, 31) * mm, "end": v(-31, 0) * mm, "construction": true});
            skCircle(sketch, "E62", {"center": v(-15.5, 15.5) * mm, "radius": 11.5 * mm});
            skSolve(sketch);
        }
        {
            var Q0;
            Q0 = qSketchRegion(id + "F31", true);
            extrude(context, id + "F32", {"entities" : qUnion([Q0]), "operationType" : NewBodyOperationType.REMOVE, "oppositeDirection" : true, "depth" : 2.5 * mm});
        }
    });
